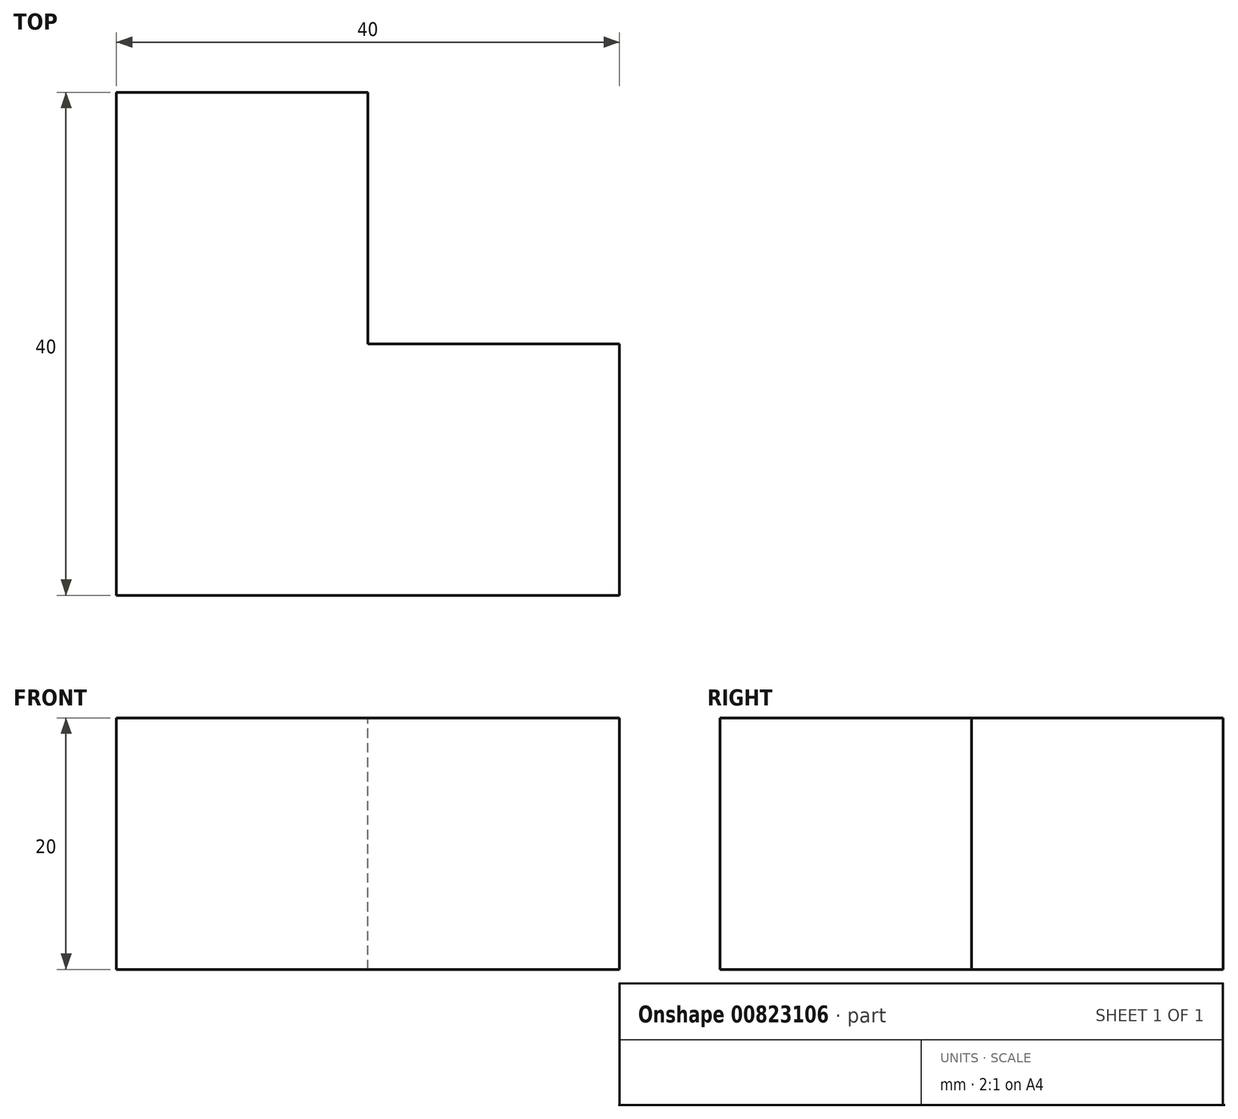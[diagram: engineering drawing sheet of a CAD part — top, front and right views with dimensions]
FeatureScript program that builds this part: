
annotation { "Feature Type Name" : "Feature", "Feature Type Description" : "" }
export const myFeature = defineFeature(function(context is Context, id is Id, definition is map)
    precondition{}
    {
        {
            var Q0;
            Q0=qCreatedBy(makeId("Front.planeOp"),FACE);
            var sketch = newSketch(context, id + "F0", { "sketchPlane" : qUnion([Q0])});
            skLineSegment(sketch, "E0.bottom", {"start": v(0, 0) * mm, "end": v(20, 0) * mm});
            skLineSegment(sketch, "E0.top", {"start": v(0, 20) * mm, "end": v(20, 20) * mm});
            skLineSegment(sketch, "E0.left", {"start": v(0, 0) * mm, "end": v(0, 20) * mm});
            skLineSegment(sketch, "E0.right", {"start": v(20, 0) * mm, "end": v(20, 20) * mm});
            skSolve(sketch);
        }
        {
            var Q0;
            Q0 = qSketchRegion(id + "F0", true);
            extrude(context, id + "F1", {"entities" : qUnion([Q0]), "depth" : 40 * mm, "offsetDistance" : 25.4 * mm});
        }
        {
            var Q0;
            Q0=makeQuery(id+"F1.opExtrude","SWEPT_FACE",FACE,{"disambiguationData":[OSD([sQuery(id+"F0.wireOp",EDGE,"E0.right")])]});
            var sketch = newSketch(context, id + "F2", { "sketchPlane" : qUnion([Q0])});
            skLineSegment(sketch, "E1.bottom", {"start": v(-40, 0) * mm, "end": v(-20, 0) * mm});
            skLineSegment(sketch, "E1.top", {"start": v(-40, 20) * mm, "end": v(-20, 20) * mm});
            skLineSegment(sketch, "E1.left", {"start": v(-40, 0) * mm, "end": v(-40, 20) * mm});
            skLineSegment(sketch, "E1.right", {"start": v(-20, 0) * mm, "end": v(-20, 20) * mm});
            skSolve(sketch);
        }
        {
            var Q0;
            Q0=makeQuery(id+"F2.imprint","IMPRINT",FACE,{"disambiguationData":[TD([[makeQuery(id+"F2.imprint","IMPRINT",EDGE,{"derivedFrom":sQuery(id+"F2.wireOp",EDGE,"E1.bottom")}),1.0]])]});
            extrude(context, id + "F3", {"entities" : qUnion([Q0]), "operationType" : NewBodyOperationType.ADD, "depth" : 20 * mm, "offsetDistance" : 25.4 * mm});
        }
    });
